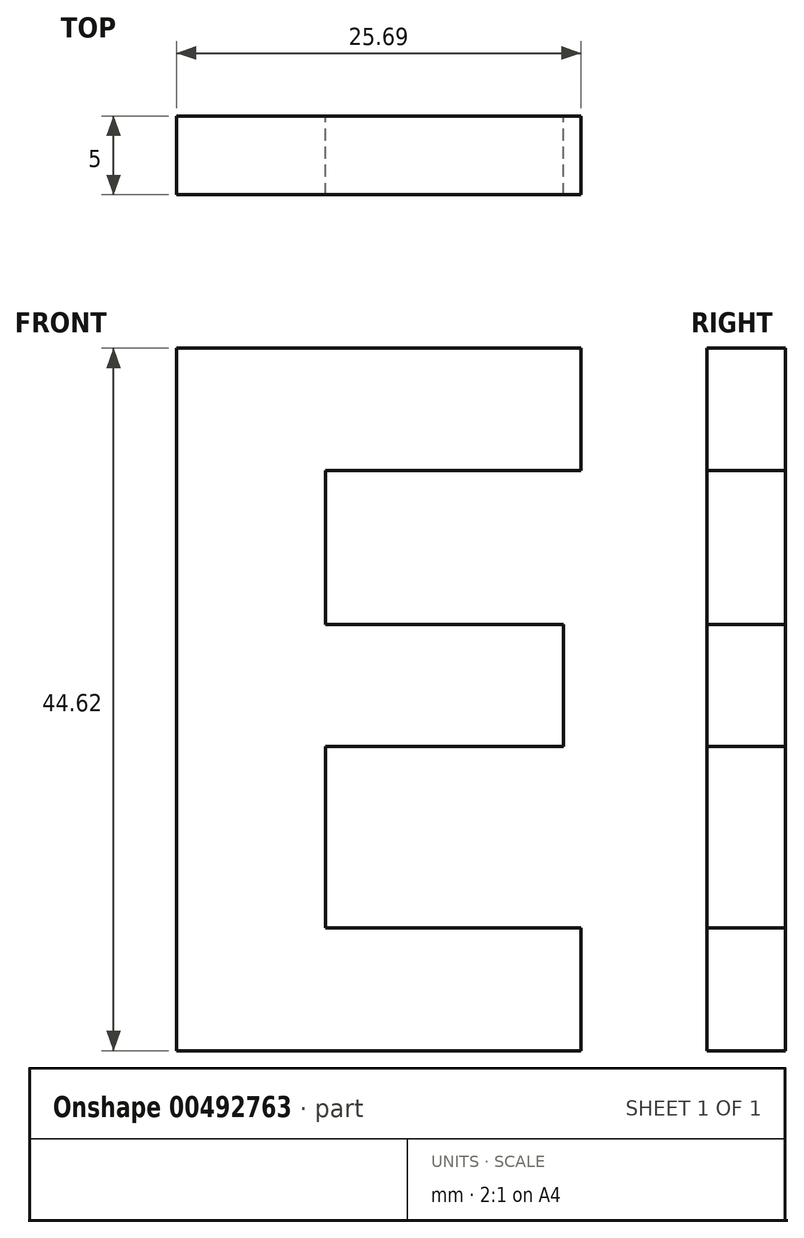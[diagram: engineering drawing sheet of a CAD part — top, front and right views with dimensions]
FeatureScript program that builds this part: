
annotation { "Feature Type Name" : "Feature", "Feature Type Description" : "" }
export const myFeature = defineFeature(function(context is Context, id is Id, definition is map)
    precondition{}
    {
        {
            var Q0;
            Q0=qCreatedBy(makeId("Front.planeOp"),FACE);
            var sketch = newSketch(context, id + "F0", { "sketchPlane" : qUnion([Q0])});
            skText(sketch, "E0", { "text": "E", "fontName": "OpenSans-Bold.ttf"});
            const initialGuessF0  = {"E0": [-0.06879, 0.01535, 1, 0, 0.045]};
            skSetInitialGuess(sketch, initialGuessF0);
            skSolve(sketch);
        }
        {
            var Q0;
            Q0=makeQuery(id+"F0.imprint","IMPRINT",FACE,{"disambiguationData":[TD([[makeQuery(id+"F0.imprint","IMPRINT",EDGE,{"derivedFrom":sQuery(id+"F0.wireOp",EDGE,"E0.sketch_text.stroke-0")}),-1.0]])]});
            extrude(context, id + "F1", {"entities" : qUnion([Q0]), "depth" : 5 * mm});
        }
    });
